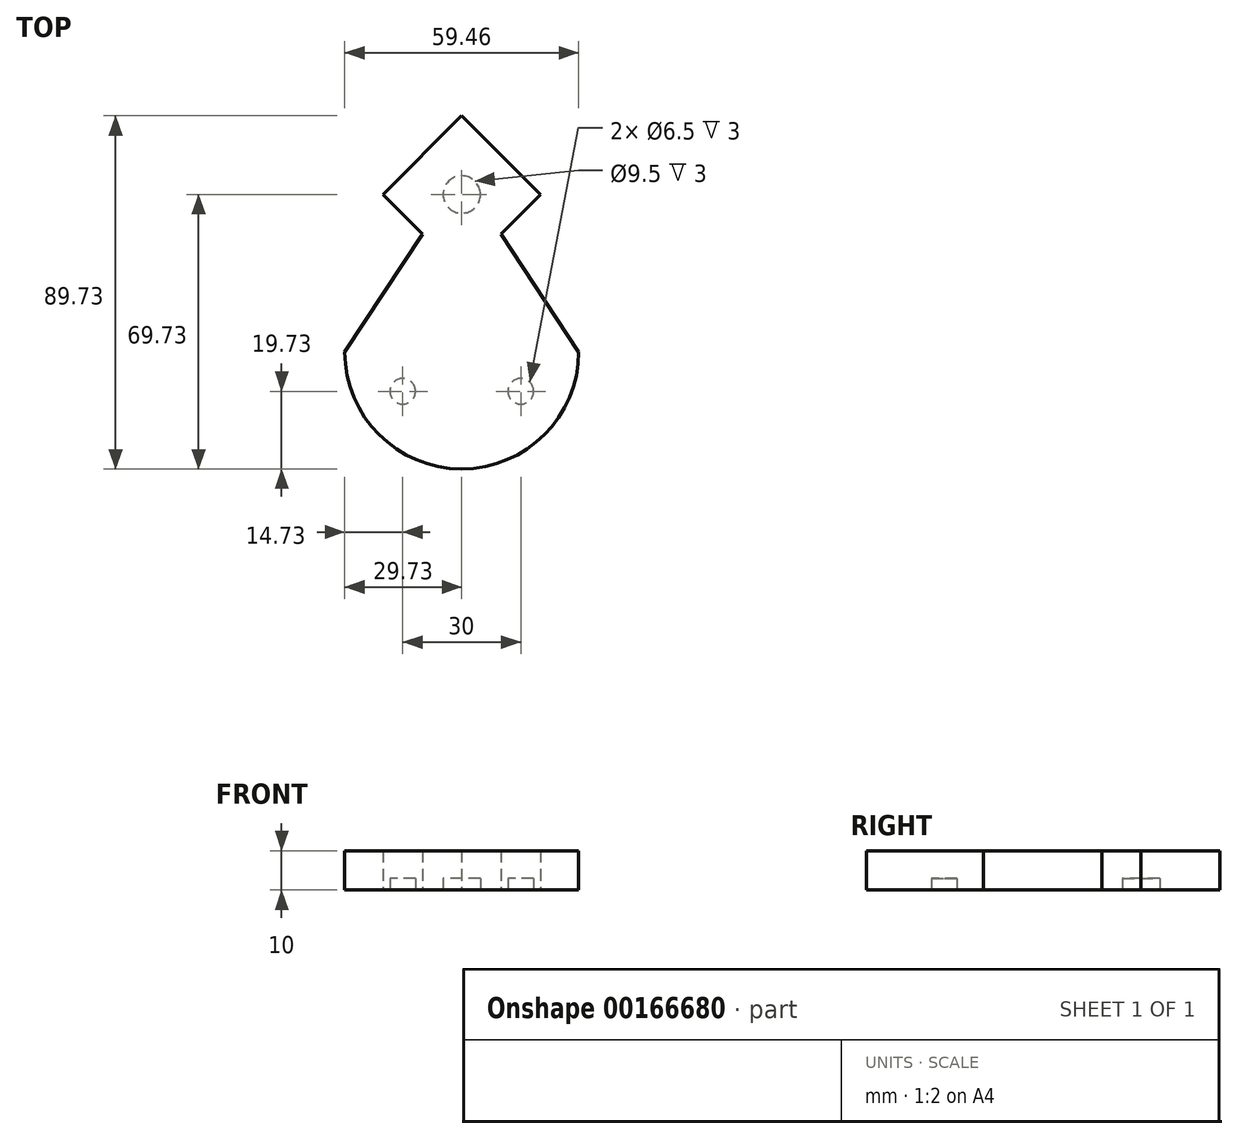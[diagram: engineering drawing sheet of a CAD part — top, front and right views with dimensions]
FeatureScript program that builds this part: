
annotation { "Feature Type Name" : "Feature", "Feature Type Description" : "" }
export const myFeature = defineFeature(function(context is Context, id is Id, definition is map)
    precondition{}
    {
        {
            var Q0;
            Q0=qCreatedBy(makeId("Top.planeOp"),FACE);
            var sketch = newSketch(context, id + "F0", { "sketchPlane" : qUnion([Q0])});
            skLineSegment(sketch, "E0.bottom", {"start": v(20, 0) * mm, "end": v(0, -20) * mm});
            skLineSegment(sketch, "E0.top", {"start": v(0, 20) * mm, "end": v(-20, 0) * mm});
            skLineSegment(sketch, "E0.left", {"start": v(20, 0) * mm, "end": v(0, 20) * mm});
            skLineSegment(sketch, "E0.right", {"start": v(0, -20) * mm, "end": v(-20, 0) * mm});
            skPoint(sketch, "E0.middle", {"position": v(0, 0) * mm});
            skLineSegment(sketch, "E1", {"start": v(-10, -10) * mm, "end": v(-29.73, -40) * mm});
            skArc(sketch, "E2", {"start": v(-29.73, -40) * mm, "mid": v(0, -69.73) * mm, "end": v(29.73, -40) * mm});
            skLineSegment(sketch, "E3", {"start": v(29.73, -40) * mm, "end": v(10, -10) * mm});
            skSolve(sketch);
        }
        {
            var Q0;
            Q0 = qSketchRegion(id + "F0", true);
            extrude(context, id + "F1", {"entities" : qUnion([Q0]), "depth" : 10 * mm});
        }
        {
            var Q0;
            Q0=qCreatedBy(makeId("Top.planeOp"),FACE);
            var sketch = newSketch(context, id + "F2", { "sketchPlane" : qUnion([Q0])});
            skCircle(sketch, "E4", {"center": v(0, 0) * mm, "radius": 4.75 * mm});
            skCircle(sketch, "E5", {"center": v(15, -50) * mm, "radius": 3.25 * mm});
            skCircle(sketch, "E6", {"center": v(-15, -50) * mm, "radius": 3.25 * mm});
            skSolve(sketch);
        }
        {
            var Q0;
            Q0 = qSketchRegion(id + "F2", true);
            extrude(context, id + "F3", {"entities" : qUnion([Q0]), "operationType" : NewBodyOperationType.REMOVE, "depth" : 3 * mm});
        }
    });
